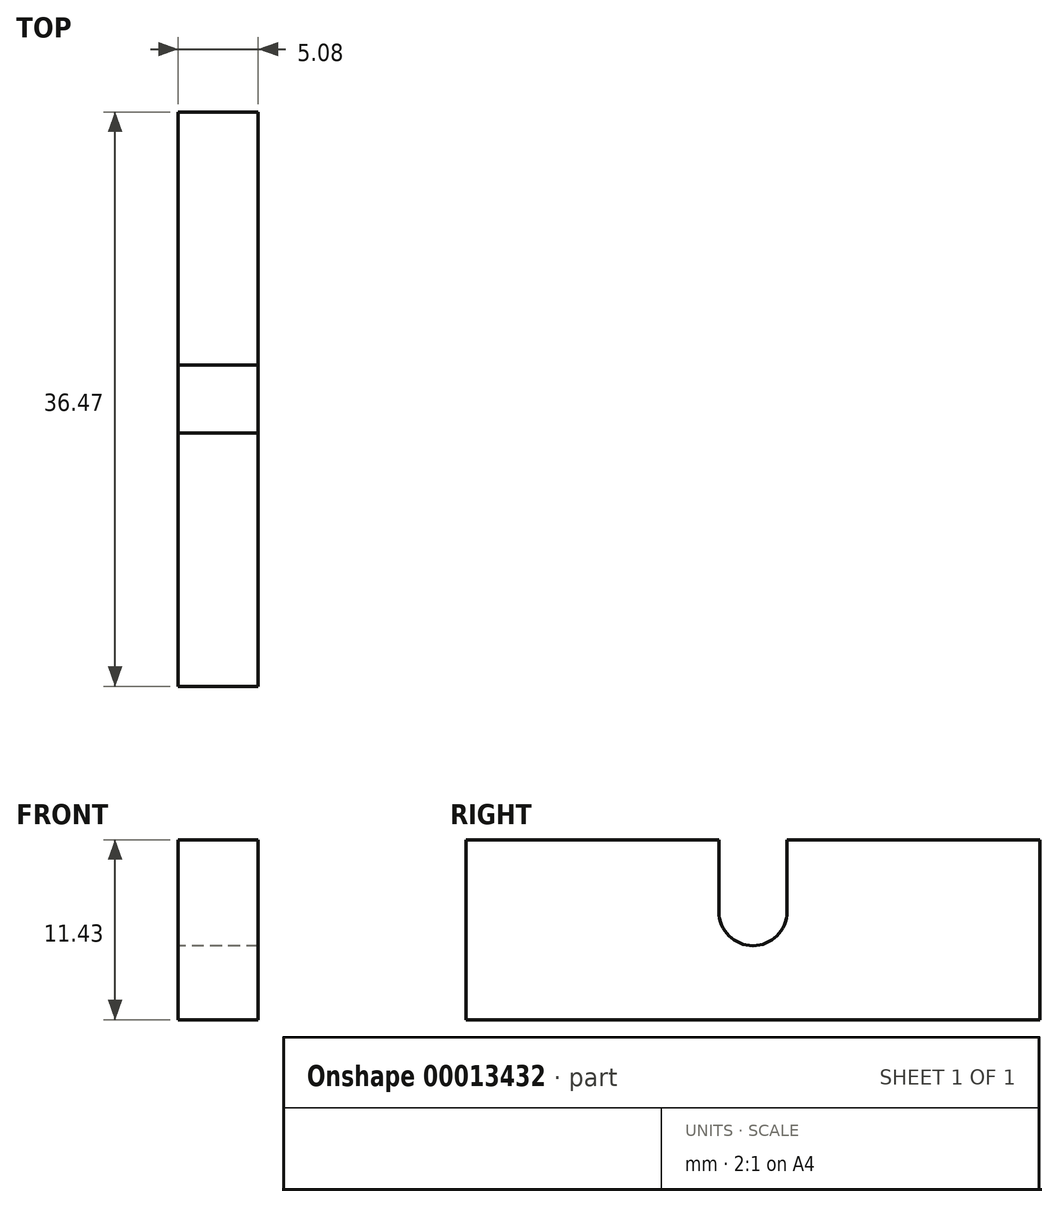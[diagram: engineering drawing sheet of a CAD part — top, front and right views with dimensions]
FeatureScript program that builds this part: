
annotation { "Feature Type Name" : "Feature", "Feature Type Description" : "" }
export const myFeature = defineFeature(function(context is Context, id is Id, definition is map)
    precondition{}
    {
        {
            var Q0;
            Q0=qCreatedBy(makeId("Right.planeOp"),FACE);
            var sketch = newSketch(context, id + "F0", { "sketchPlane" : qUnion([Q0])});
            skLineSegment(sketch, "E0.bottom", {"start": v(0, 0) * mm, "end": v(36.47, 0) * mm});
            skLineSegment(sketch, "E0.top", {"start": v(0, 11.43) * mm, "end": v(16.08, 11.43) * mm});
            skLineSegment(sketch, "E0.left", {"start": v(0, 0) * mm, "end": v(0, 11.43) * mm});
            skLineSegment(sketch, "E0.right", {"start": v(36.47, 0) * mm, "end": v(36.47, 11.43) * mm});
            skLineSegment(sketch, "E1", {"start": v(16.08, 11.43) * mm, "end": v(16.08, 6.86) * mm});
            skLineSegment(sketch, "E2.1.0.0", {"start": v(20.4, 11.43) * mm, "end": v(20.4, 6.86) * mm});
            skLineSegment(sketch, "E2.direction1", {"start": v(16.08, 6.86) * mm, "end": v(20.4, 6.86) * mm, "construction": true});
            skArc(sketch, "E3", {"start": v(16.08, 6.86) * mm, "mid": v(18.24, 4.7) * mm, "end": v(20.4, 6.86) * mm});
            skLineSegment(sketch, "E4.trimOffspring", {"start": v(20.4, 11.43) * mm, "end": v(36.47, 11.43) * mm});
            skSolve(sketch);
        }
        {
            var Q0;
            Q0 = qSketchRegion(id + "F0", true);
            extrude(context, id + "F1", {"entities" : qUnion([Q0]), "depth" : 5.08 * mm});
        }
    });
